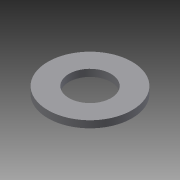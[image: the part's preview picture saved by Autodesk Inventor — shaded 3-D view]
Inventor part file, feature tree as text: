
AUTODESK INVENTOR PART (.ipt)
format: ipt  version: 2013 (Build 170138000, 138)  size: 72,704 bytes
history: native  units: in
note: dims shown in document units (in); Inventor stores cm internally (conversion verified against a paired STEP export)
features: extrude x1, sketch x1
ambient origin geometry x8: Origin, YZ Plane, XZ Plane, XY Plane, X Axis, Y Axis, Z Axis, Center Point
bodies: Solid1 (feature_tree)
feature tree (2):
  extrude  "Extrusion1"  Depth=0.375in
  sketch  "Sketch1"  dims[d0=0.75in d1=0.375in d2=0.0625in d3=0.0in]
